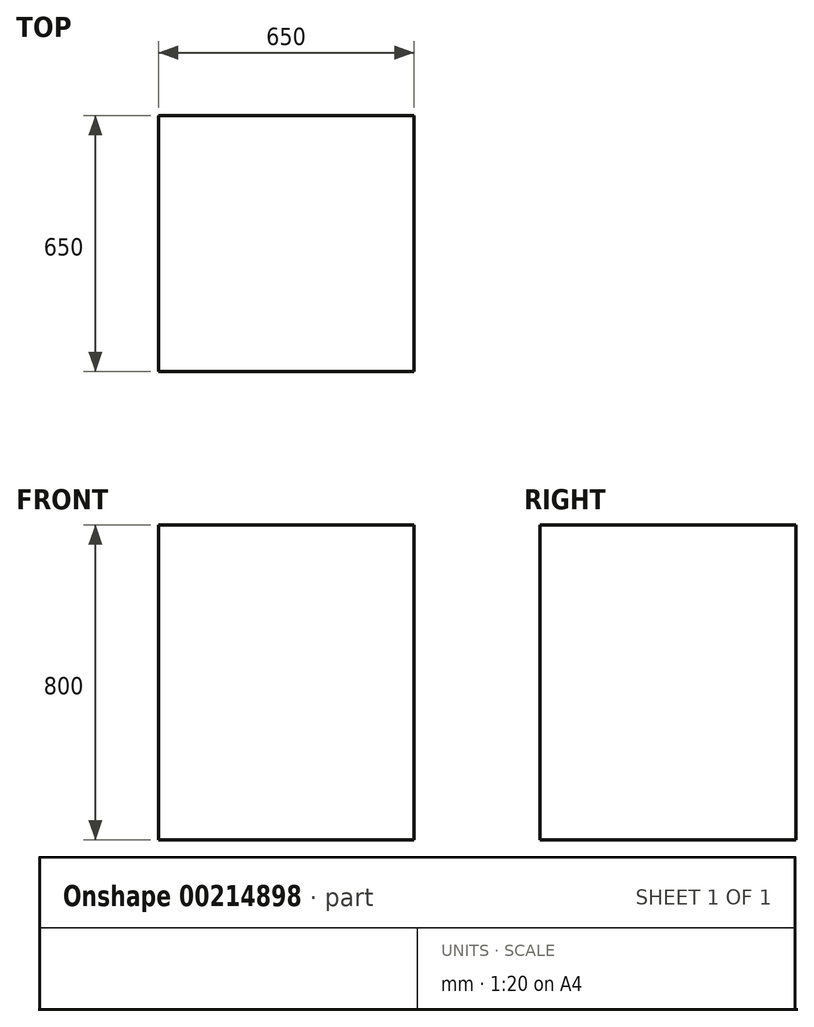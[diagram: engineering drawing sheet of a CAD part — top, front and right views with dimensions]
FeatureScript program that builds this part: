
annotation { "Feature Type Name" : "Feature", "Feature Type Description" : "" }
export const myFeature = defineFeature(function(context is Context, id is Id, definition is map)
    precondition{}
    {
        {
            var Q0;
            Q0=qCreatedBy(makeId("Top.planeOp"),FACE);
            var sketch = newSketch(context, id + "F0", { "sketchPlane" : qUnion([Q0])});
            skLineSegment(sketch, "E0.bottom", {"start": v(325, 325) * mm, "end": v(-325, 325) * mm});
            skLineSegment(sketch, "E0.top", {"start": v(325, -325) * mm, "end": v(-325, -325) * mm});
            skLineSegment(sketch, "E0.left", {"start": v(325, 325) * mm, "end": v(325, -325) * mm});
            skLineSegment(sketch, "E0.right", {"start": v(-325, 325) * mm, "end": v(-325, -325) * mm});
            skPoint(sketch, "E0.middle", {"position": v(0, 0) * mm});
            skSolve(sketch);
        }
        {
            var Q0;
            Q0 = qSketchRegion(id + "F0", true);
            extrude(context, id + "F1", {"entities" : qUnion([Q0]), "depth" : 800 * mm});
        }
    });
